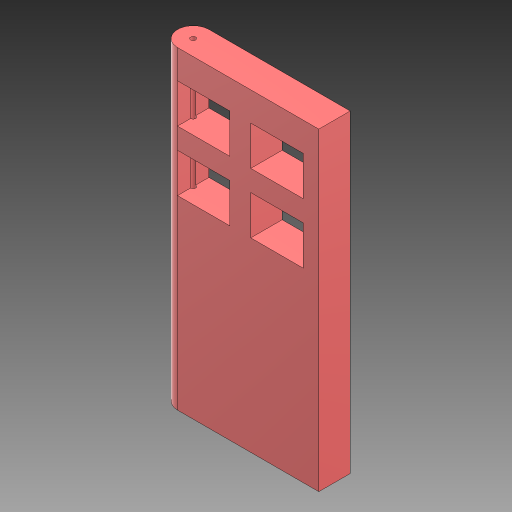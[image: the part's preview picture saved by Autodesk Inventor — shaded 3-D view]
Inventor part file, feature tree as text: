
AUTODESK INVENTOR PART (.ipt)
format: ipt  version: 2023 (Build 270158000, 158)  size: 499,712 bytes
history: native  units: mm
features: sketch x3, other x2, extrude x2, hole x1
ambient origin geometry x8: Origin, YZ Plane, XZ Plane, XY Plane, X Axis, Y Axis, Z Axis, Center Point
bodies: Body1 (feature_tree)
feature tree (8):
  other  "Těleso1"
  extrude  "Vysunutí1"  Depth=30.0mm
  extrude  "Vysunutí2"  Depth=60.0mm
  other  "Plné kulaté zaoblení1"
  hole  "Díra1"  [1 undecoded]
  sketch  "Náčrt1"
  sketch  "Náčrt2"
  sketch  "Náčrt3"
note: 1 required parameter value undecoded (feature->parameter linkage not recoverable at this tier; creation-order binding heuristic only, values carry confidence <= 0.55)
